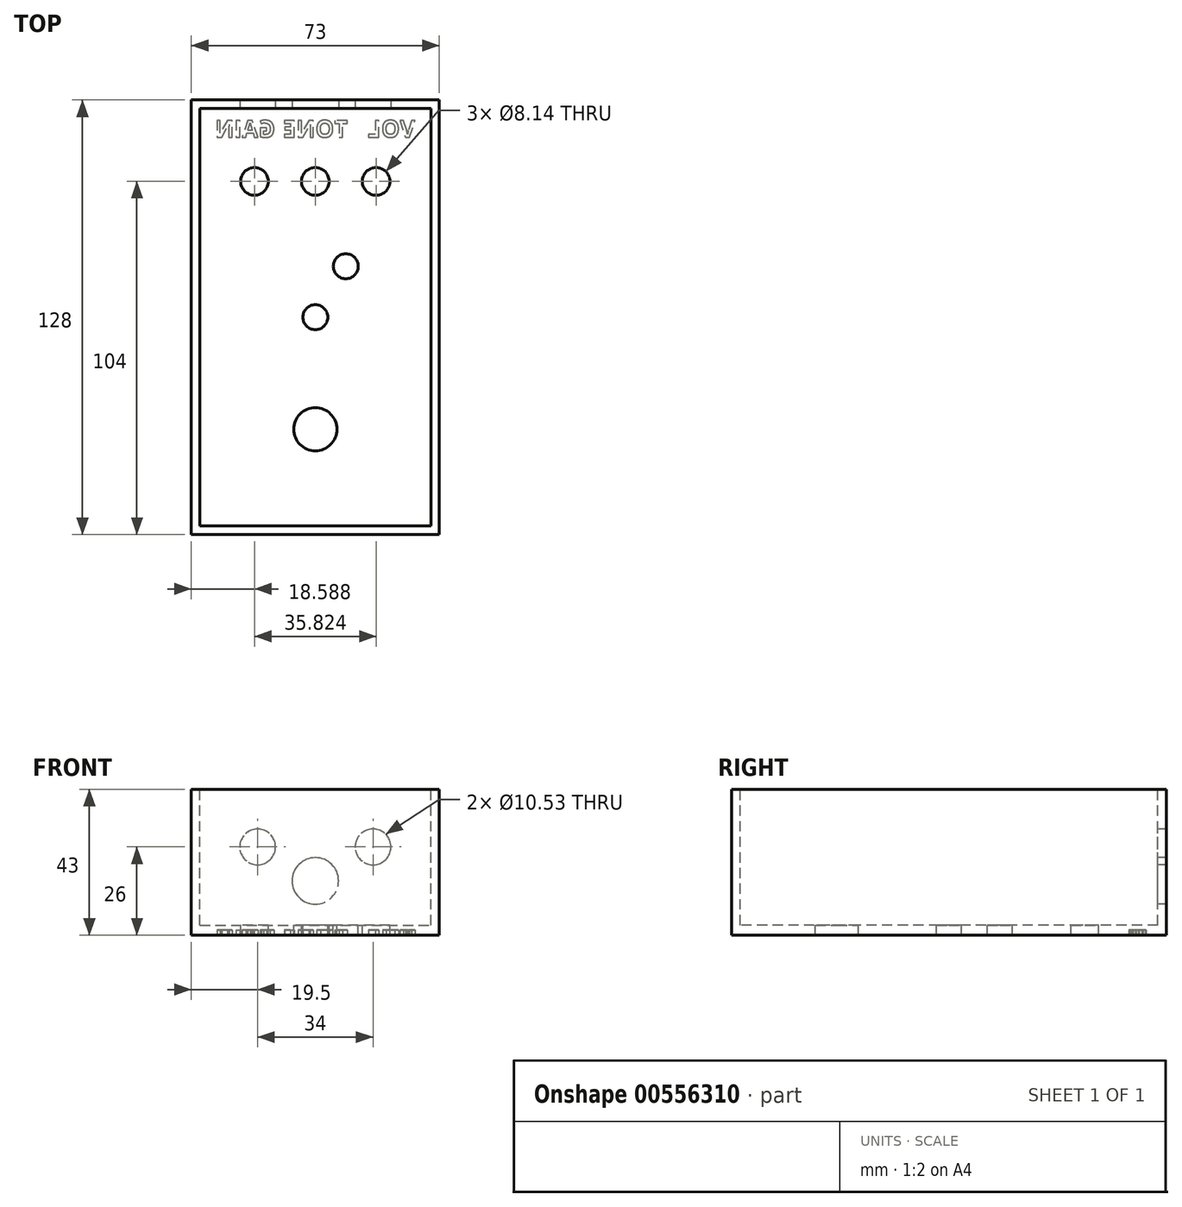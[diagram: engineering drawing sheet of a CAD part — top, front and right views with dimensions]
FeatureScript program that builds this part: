
annotation { "Feature Type Name" : "Feature", "Feature Type Description" : "" }
export const myFeature = defineFeature(function(context is Context, id is Id, definition is map)
    precondition{}
    {
        {
            var Q0;
            Q0=qCreatedBy(makeId("Top.planeOp"),FACE);
            var sketch = newSketch(context, id + "F0", { "sketchPlane" : qUnion([Q0])});
            skLineSegment(sketch, "E0.bottom", {"start": v(-36.5, 64) * mm, "end": v(36.5, 64) * mm});
            skLineSegment(sketch, "E0.top", {"start": v(-36.5, -64) * mm, "end": v(36.5, -64) * mm});
            skLineSegment(sketch, "E0.left", {"start": v(-36.5, 64) * mm, "end": v(-36.5, -64) * mm});
            skLineSegment(sketch, "E0.right", {"start": v(36.5, 64) * mm, "end": v(36.5, -64) * mm});
            skSolve(sketch);
        }
        {
            var Q0;
            Q0=makeQuery(id+"F0.imprint","IMPRINT",FACE,{"disambiguationData":[TD([[makeQuery(id+"F0.imprint","IMPRINT",EDGE,{"derivedFrom":sQuery(id+"F0.wireOp",EDGE,"E0.bottom")}),-1.0]])]});
            extrude(context, id + "F1", {"entities" : qUnion([Q0]), "depth" : 43 * mm, "offsetDistance" : 25 * mm});
        }
        {
            var Q0;
            Q0=makeQuery(id+"F1.opExtrude","CAP_FACE",FACE,{"disambiguationData":[OSD([sQuery(id+"F0.wireOp",EDGE,"E0.bottom"),sQuery(id+"F0.wireOp",EDGE,"E0.top"),sQuery(id+"F0.wireOp",EDGE,"E0.left"),sQuery(id+"F0.wireOp",EDGE,"E0.right")])],"isStart":false});
            var sketch = newSketch(context, id + "F2", { "sketchPlane" : qUnion([Q0])});
            skLineSegment(sketch, "E1.bottom", {"start": v(-34, 61.5) * mm, "end": v(34, 61.5) * mm});
            skLineSegment(sketch, "E1.top", {"start": v(-34, -61.5) * mm, "end": v(34, -61.5) * mm});
            skLineSegment(sketch, "E1.left", {"start": v(-34, 61.5) * mm, "end": v(-34, -61.5) * mm});
            skLineSegment(sketch, "E1.right", {"start": v(34, 61.5) * mm, "end": v(34, -61.5) * mm});
            skSolve(sketch);
        }
        {
            var Q0;
            Q0=makeQuery(id+"F2.imprint","IMPRINT",FACE,{"disambiguationData":[TD([[makeQuery(id+"F2.imprint","IMPRINT",EDGE,{"derivedFrom":sQuery(id+"F2.wireOp",EDGE,"E1.bottom")}),-1.0]])]});
            extrude(context, id + "F3", {"entities" : qUnion([Q0]), "operationType" : NewBodyOperationType.REMOVE, "oppositeDirection" : true, "depth" : 40 * mm, "offsetDistance" : 25 * mm});
        }
        {
            var Q0;
            Q0=makeQuery(id+"F3.boolean.opBoolean","COPY",FACE,{"derivedFrom":makeQuery(id+"F3.opExtrude","CAP_FACE",FACE,{"disambiguationData":[OSD([sQuery(id+"F2.wireOp",EDGE,"E1.bottom"),sQuery(id+"F2.wireOp",EDGE,"E1.top"),sQuery(id+"F2.wireOp",EDGE,"E1.left"),sQuery(id+"F2.wireOp",EDGE,"E1.right")])],"isStart":false})});
            var sketch = newSketch(context, id + "F4", { "sketchPlane" : qUnion([Q0])});
            skCircle(sketch, "E2", {"center": v(-17.91, 40) * mm, "radius": 4.07 * mm});
            skCircle(sketch, "E3", {"center": v(0, 40) * mm, "radius": 4.07 * mm});
            skCircle(sketch, "E4", {"center": v(17.91, 40) * mm, "radius": 4.07 * mm});
            skCircle(sketch, "E5", {"center": v(0, -33) * mm, "radius": 6.35 * mm});
            skLineSegment(sketch, "E6", {"start": v(17.91, 40) * mm, "end": v(0, 40) * mm, "construction": true});
            skLineSegment(sketch, "E7", {"start": v(8.96, 40) * mm, "end": v(8.96, 15.16) * mm, "construction": true});
            skCircle(sketch, "E8", {"center": v(8.96, 15) * mm, "radius": 3.67 * mm});
            skCircle(sketch, "E9", {"center": v(0, 0) * mm, "radius": 3.67 * mm});
            skSolve(sketch);
        }
        {
            var Q0;
            Q0=qSketchRegion(id+"F4",true);
            extrude(context, id + "F5", {"entities" : qUnion([Q0]), "operationType" : NewBodyOperationType.REMOVE, "oppositeDirection" : true, "depth" : 25 * mm, "offsetDistance" : 25 * mm});
        }
        {
            var Q0;
            Q0=makeQuery(id+"F3.boolean.opBoolean","COPY",FACE,{"derivedFrom":makeQuery(id+"F3.opExtrude","SWEPT_FACE",FACE,{"disambiguationData":[OSD([sQuery(id+"F2.wireOp",EDGE,"E1.bottom")])]})});
            var sketch = newSketch(context, id + "F6", { "sketchPlane" : qUnion([Q0])});
            skCircle(sketch, "E10", {"center": v(0, 16) * mm, "radius": 6.85 * mm});
            skCircle(sketch, "E11", {"center": v(17, 26) * mm, "radius": 5.26 * mm});
            skCircle(sketch, "E12", {"center": v(-17, 26) * mm, "radius": 5.26 * mm});
            skSolve(sketch);
        }
        {
            var Q0;
            Q0=qSketchRegion(id+"F6",true);
            extrude(context, id + "F7", {"entities" : qUnion([Q0]), "operationType" : NewBodyOperationType.REMOVE, "oppositeDirection" : true, "depth" : 25 * mm, "offsetDistance" : 25 * mm});
        }
        {
            var Q0;
            Q0=qCreatedBy(makeId("Front.planeOp"),FACE);
            cPlane(context, id + "F8", {"entities" : qUnion([Q0]), "cplaneType" : CPlaneType.OFFSET, "offset" : 38 * mm, "width" : 150 * mm, "height" : 150 * mm});
        }
        {
            var Q0;
            Q0=makeQuery(id+"F1.opExtrude","CAP_FACE",FACE,{"disambiguationData":[OSD([sQuery(id+"F0.wireOp",EDGE,"E0.bottom"),sQuery(id+"F0.wireOp",EDGE,"E0.top"),sQuery(id+"F0.wireOp",EDGE,"E0.left"),sQuery(id+"F0.wireOp",EDGE,"E0.right")])],"isStart":true});
            var sketch = newSketch(context, id + "F9", { "sketchPlane" : qUnion([Q0])});
            skText(sketch, "E13", { "text": "VOL", "fontName": "OpenSans-Bold.ttf"});
            skText(sketch, "E14", { "text": "TONE", "fontName": "OpenSans-Bold.ttf"});
            skText(sketch, "E15", { "text": "GAIN", "fontName": "OpenSans-Bold.ttf"});
            const initialGuessF9  = {"E13": [0.0294, -0.053, -1, 0, 0.005], "E14": [0.00956, -0.053, -1, 0, 0.005], "E15": [-0.0118, -0.053, -1, 0, 0.005]};
            skSetInitialGuess(sketch, initialGuessF9);
            skSolve(sketch);
        }
        {
            var Q0;
            Q0=qSketchRegion(id+"F9",true);
            extrude(context, id + "F10", {"entities" : qUnion([Q0]), "operationType" : NewBodyOperationType.REMOVE, "oppositeDirection" : true, "depth" : 1.5 * mm, "offsetDistance" : 25 * mm});
        }
    });
